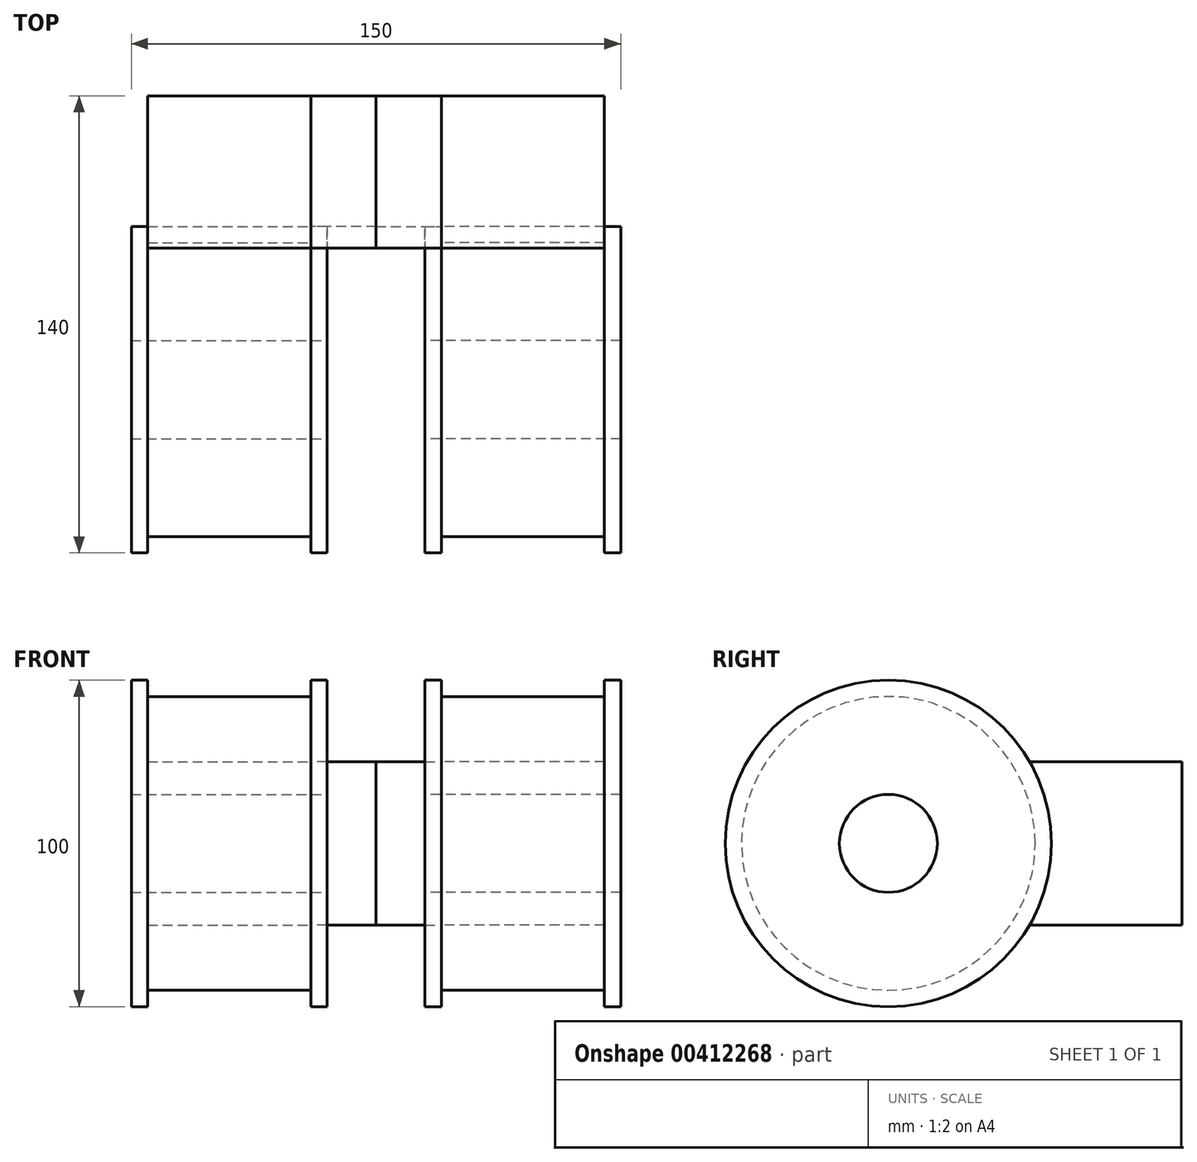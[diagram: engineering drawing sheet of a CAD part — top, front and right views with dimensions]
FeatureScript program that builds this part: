
annotation { "Feature Type Name" : "Feature", "Feature Type Description" : "" }
export const myFeature = defineFeature(function(context is Context, id is Id, definition is map)
    precondition{}
    {
        {
            var Q0;
            Q0=qCreatedBy(makeId("Right.planeOp"),FACE);
            var sketch = newSketch(context, id + "F0", { "sketchPlane" : qUnion([Q0])});
            skCircle(sketch, "E0", {"center": v(0, 0) * mm, "radius": 50 * mm});
            skCircle(sketch, "E1", {"center": v(0, 0) * mm, "radius": 45 * mm});
            skLineSegment(sketch, "E2.bottom", {"start": v(0, 25) * mm, "end": v(90, 25) * mm});
            skLineSegment(sketch, "E2.top", {"start": v(0, -25) * mm, "end": v(90, -25) * mm});
            skLineSegment(sketch, "E2.left", {"start": v(0, 25) * mm, "end": v(0, -25) * mm});
            skLineSegment(sketch, "E2.right", {"start": v(90, 25) * mm, "end": v(90, -25) * mm});
            skPoint(sketch, "E2.middle", {"position": v(45, 0) * mm});
            skCircle(sketch, "E3", {"center": v(0, 0) * mm, "radius": 15 * mm});
            skSolve(sketch);
        }
        {
            var Q0;
            {var subQ5=sQuery(id+"F0.wireOp",EDGE,"E2.left");Q0=makeQuery(id+"F0.imprint","IMPRINT",FACE,{"disambiguationData":[TD([[makeQuery(id+"F0.imprint","IMPRINT",EDGE,{"derivedFrom":subQ5}),-1.0]])]});}
            var Q1;
            {var subQ1=sQuery(id+"F0.wireOp",EDGE,"E2.bottom");var subQ7=sQuery(id+"F0.wireOp",EDGE,"E1");var subQ9=makeQuery(id+"F0.imprint","INTERSECT",VERTEX,{"derivedFrom":[subQ7,subQ1]});Q1=makeQuery(id+"F0.imprint","IMPRINT",FACE,{"disambiguationData":[TD([[makeQuery(id+"F0.imprint","IMPRINT",EDGE,{"disambiguationData":[TD([[subQ9,1.0]])],"derivedFrom":subQ7}),1.0]])]});}
            var Q2;
            Q2=sQuery(id+"F0.wireOp",EDGE,"E1");
            extrude(context, id + "F1", {"entities" : qUnion([Q0, Q1]), "surfaceEntities" : qUnion([Q2]), "depth" : 25 * mm});
        }
        {
            var Q0;
            {var subQ0=sQuery(id+"F0.wireOp",EDGE,"E2.bottom");var subQ1=sQuery(id+"F0.wireOp",EDGE,"E0");var subQ2=makeQuery(id+"F0.imprint","INTERSECT",VERTEX,{"derivedFrom":[subQ1,subQ0]});Q0=makeQuery(id+"F0.imprint","IMPRINT",FACE,{"disambiguationData":[TD([[makeQuery(id+"F0.imprint","IMPRINT",EDGE,{"disambiguationData":[TD([[subQ2,-1.0]])],"derivedFrom":subQ1}),1.0]])]});}
            var Q1;
            {var subQ5=sQuery(id+"F0.wireOp",EDGE,"E2.left");Q1=makeQuery(id+"F0.imprint","IMPRINT",FACE,{"disambiguationData":[TD([[makeQuery(id+"F0.imprint","IMPRINT",EDGE,{"derivedFrom":subQ5}),-1.0]])]});}
            var Q2;
            {var subQ1=sQuery(id+"F0.wireOp",EDGE,"E2.bottom");var subQ7=sQuery(id+"F0.wireOp",EDGE,"E1");var subQ9=makeQuery(id+"F0.imprint","INTERSECT",VERTEX,{"derivedFrom":[subQ7,subQ1]});Q2=makeQuery(id+"F0.imprint","IMPRINT",FACE,{"disambiguationData":[TD([[makeQuery(id+"F0.imprint","IMPRINT",EDGE,{"disambiguationData":[TD([[subQ9,1.0]])],"derivedFrom":subQ7}),1.0]])]});}
            var Q3;
            {var subQ0=sQuery(id+"F0.wireOp",EDGE,"E2.bottom");var subQ1=sQuery(id+"F0.wireOp",EDGE,"E0");var subQ2=makeQuery(id+"F0.imprint","INTERSECT",VERTEX,{"derivedFrom":[subQ1,subQ0]});Q3=makeQuery(id+"F0.imprint","IMPRINT",FACE,{"disambiguationData":[TD([[makeQuery(id+"F0.imprint","IMPRINT",EDGE,{"disambiguationData":[TD([[subQ2,1.0]])],"derivedFrom":subQ1}),1.0]])]});}
            extrude(context, id + "F2", {"entities" : qUnion([Q0, Q1, Q2, Q3]), "operationType" : NewBodyOperationType.ADD, "oppositeDirection" : true, "depth" : 5 * mm});
        }
        {
            var Q0;
            Q0=makeQuery(id+"F1.opExtrude","SWEPT_BODY",BODY,{"disambiguationData":[OSD([sQuery(id+"F0.wireOp",EDGE,"E1"),sQuery(id+"F0.wireOp",EDGE,"E2.bottom"),sQuery(id+"F0.wireOp",EDGE,"E2.top"),sQuery(id+"F0.wireOp",EDGE,"E2.left")])]});
            var Q1;
            Q1=makeQuery(id+"F1.opExtrude","CAP_FACE",FACE,{"disambiguationData":[OSD([sQuery(id+"F0.wireOp",EDGE,"E1"),sQuery(id+"F0.wireOp",EDGE,"E2.bottom"),sQuery(id+"F0.wireOp",EDGE,"E2.top"),sQuery(id+"F0.wireOp",EDGE,"E2.left")])],"isStart":false});
            mirror(context, id + "F3", {"operationType" : NewBodyOperationType.ADD, "entities" : qUnion([Q0]), "mirrorPlane" : qUnion([Q1])});
        }
        {
            var Q0;
            {var subQ5=sQuery(id+"F0.wireOp",EDGE,"E2.right");Q0=makeQuery(id+"F0.imprint","IMPRINT",FACE,{"disambiguationData":[TD([[makeQuery(id+"F0.imprint","IMPRINT",EDGE,{"derivedFrom":subQ5}),-1.0]])]});}
            extrude(context, id + "F4", {"entities" : qUnion([Q0]), "operationType" : NewBodyOperationType.ADD, "depth" : 50 * mm});
        }
        {
            var Q0;
            {var subQ5=sQuery(id+"F0.wireOp",EDGE,"E2.right");Q0=makeQuery(id+"F0.imprint","IMPRINT",FACE,{"disambiguationData":[TD([[makeQuery(id+"F0.imprint","IMPRINT",EDGE,{"derivedFrom":subQ5}),-1.0]])]});}
            var sketch = newSketch(context, id + "F5", { "sketchPlane" : qUnion([Q0])});
            skSolve(sketch);
        }
        {
            var Q0;
            Q0 = qSketchRegion(id + "F5", true);
            var Q1;
            {var subQ5=sQuery(id+"F0.wireOp",EDGE,"E2.right");Q1=makeQuery(id+"F0.imprint","IMPRINT",FACE,{"disambiguationData":[TD([[makeQuery(id+"F0.imprint","IMPRINT",EDGE,{"derivedFrom":subQ5}),-1.0]])]});}
            extrude(context, id + "F6", {"entities" : qUnion([Q0, Q1]), "oppositeDirection" : true, "depth" : 20 * mm});
        }
        {
            var Q0;
            Q0=makeQuery(id+"F1.opExtrude","SWEPT_BODY",BODY,{"disambiguationData":[OSD([sQuery(id+"F0.wireOp",EDGE,"E1"),sQuery(id+"F0.wireOp",EDGE,"E3")])]});
            var Q1;
            Q1=makeQuery(id+"F4.opExtrude","SWEPT_BODY",BODY,{"disambiguationData":[OSD([sQuery(id+"F0.wireOp",EDGE,"E0"),sQuery(id+"F0.wireOp",EDGE,"E2.bottom"),sQuery(id+"F0.wireOp",EDGE,"E2.top"),sQuery(id+"F0.wireOp",EDGE,"E2.right")])]});
            var Q2;
            Q2=makeQuery(id+"F6.opExtrude","SWEPT_BODY",BODY,{"disambiguationData":[OSD([sQuery(id+"F0.wireOp",EDGE,"E0"),sQuery(id+"F0.wireOp",EDGE,"E2.bottom"),sQuery(id+"F0.wireOp",EDGE,"E2.top"),sQuery(id+"F0.wireOp",EDGE,"E2.right")])]});
            var Q3;
            Q3=makeQuery(id+"F6.opExtrude","CAP_FACE",FACE,{"disambiguationData":[OSD([sQuery(id+"F0.wireOp",EDGE,"E0"),sQuery(id+"F0.wireOp",EDGE,"E2.bottom"),sQuery(id+"F0.wireOp",EDGE,"E2.top"),sQuery(id+"F0.wireOp",EDGE,"E2.right")])],"isStart":false});
            mirror(context, id + "F7", {"entities" : qUnion([Q0, Q1, Q2]), "mirrorPlane" : qUnion([Q3])});
        }
    });
